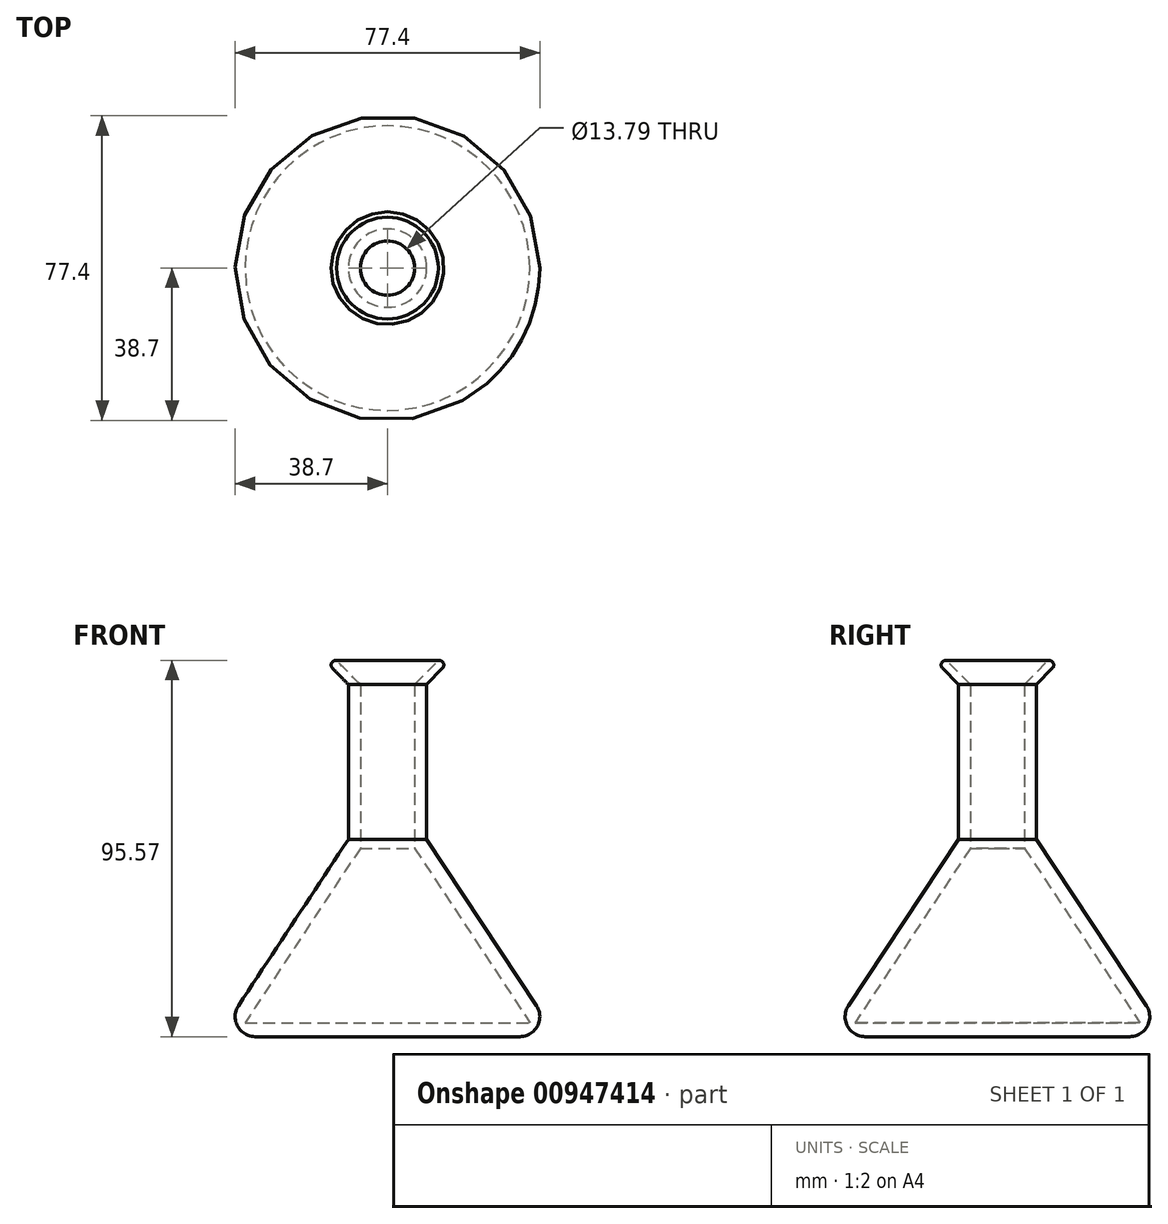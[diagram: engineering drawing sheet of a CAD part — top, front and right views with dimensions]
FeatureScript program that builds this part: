
annotation { "Feature Type Name" : "Feature", "Feature Type Description" : "" }
export const myFeature = defineFeature(function(context is Context, id is Id, definition is map)
    precondition{}
    {
        {
            var Q0;
            Q0=qCreatedBy(makeId("Front.planeOp"),FACE);
            var sketch = newSketch(context, id + "F0", { "sketchPlane" : qUnion([Q0])});
            skLineSegment(sketch, "E0", {"start": v(0, 45.42) * mm, "end": v(15.86, 45.42) * mm});
            skLineSegment(sketch, "E1", {"start": v(15.86, 45.42) * mm, "end": v(9.95, 39.32) * mm});
            skLineSegment(sketch, "E2", {"start": v(9.95, 39.32) * mm, "end": v(9.95, 0) * mm});
            skLineSegment(sketch, "E3", {"start": v(9.95, 0) * mm, "end": v(43.06, -50.15) * mm});
            skLineSegment(sketch, "E4", {"start": v(43.06, -50.15) * mm, "end": v(0, -50.15) * mm});
            skLineSegment(sketch, "E5", {"start": v(0, -50.15) * mm, "end": v(0, -46.6) * mm});
            skLineSegment(sketch, "E6", {"start": v(0, -46.6) * mm, "end": v(36.16, -46.6) * mm});
            skLineSegment(sketch, "E7", {"start": v(36.16, -46.6) * mm, "end": v(6.9, -2.27) * mm});
            skLineSegment(sketch, "E8", {"start": v(6.9, -2.27) * mm, "end": v(6.9, 39.32) * mm});
            skLineSegment(sketch, "E9", {"start": v(6.9, 39.32) * mm, "end": v(12.9, 45.42) * mm});
            skPoint(sketch, "E9.endSnap0", {"position": v(12.9, 42.37) * mm});
            skLineSegment(sketch, "E10", {"start": v(12.9, 45.42) * mm, "end": v(15.86, 45.42) * mm});
            skSolve(sketch);
        }
        {
            var Q0;
            {var subQ0=sQuery(id+"F0.wireOp",EDGE,"E1");Q0=makeQuery(id+"F0.imprint","IMPRINT",FACE,{"disambiguationData":[TD([[makeQuery(id+"F0.imprint","IMPRINT",EDGE,{"derivedFrom":subQ0}),-1.0]])]});}
            var Q1;
            Q1=sQuery(id+"F0.wireOp",EDGE,"E5");
            revolve(context, id + "F1", {"surfaceOperationType" : NewSurfaceOperationType.NEW, "entities" : qUnion([Q0]), "axis" : qUnion([Q1]), "revolveType" : RevolveType.FULL});
        }
        {
            var Q0;
            Q0=makeQuery(id+"F1.opRevolve","SWEPT_EDGE",EDGE,{"disambiguationData":[OSD([sQuery(id+"F0.wireOp",EDGE,"E3"),sQuery(id+"F0.wireOp",EDGE,"E4")])]});
            fillet(context, id + "F2", {"entities" : qUnion([Q0]), "radius" : 5.08 * mm, "tangentPropagation" : true, "allowEdgeOverflow" : false});
        }
        {
            var Q0;
            Q0=makeQuery(id+"F1.opRevolve","SWEPT_EDGE",EDGE,{"disambiguationData":[OSD([sQuery(id+"F0.wireOp",EDGE,"E0"),sQuery(id+"F0.wireOp",EDGE,"E1")])]});
            fillet(context, id + "F3", {"entities" : qUnion([Q0]), "radius" : 1.14 * mm, "tangentPropagation" : true, "allowEdgeOverflow" : false});
        }
    });
